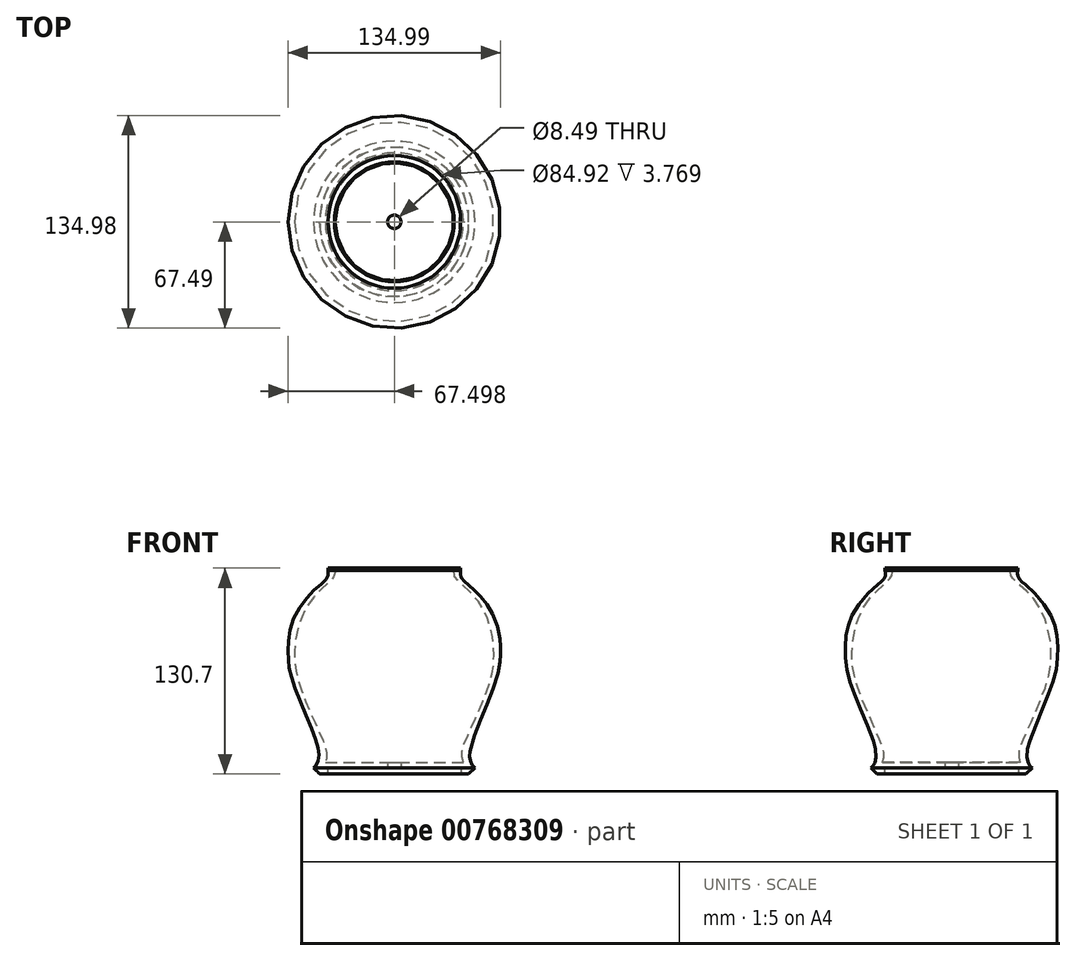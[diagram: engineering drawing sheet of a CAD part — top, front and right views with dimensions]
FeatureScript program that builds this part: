
annotation { "Feature Type Name" : "Feature", "Feature Type Description" : "" }
export const myFeature = defineFeature(function(context is Context, id is Id, definition is map)
    precondition{}
    {
        {
            var Q0;
            Q0=qCreatedBy(makeId("Front.planeOp"),FACE);
            var sketch = newSketch(context, id + "F0", { "sketchPlane" : qUnion([Q0])});
            skFitSpline(sketch, "E0", {"points": [v(87.17, 77.75) * mm, v(87.17, 72.81) * mm, v(102.26, 57.15) * mm, v(112.41, 25.24) * mm, v(108.06, 0) * mm, v(95.88, -28.43) * mm, v(92.1, -40.03) * mm, v(92.98, -45.55) * mm], "startDerivative": vector(-17.62, -61.82) * mm, "endDerivative": vector(18.04, -64.32) * mm});
            skLineSegment(sketch, "E1", {"start": v(92.98, -45.55) * mm, "end": v(53.4, -45.55) * mm});
            skLineSegment(sketch, "E2", {"start": v(53.4, -45.55) * mm, "end": v(53.4, -49.19) * mm});
            skLineSegment(sketch, "E3", {"start": v(53.4, -49.19) * mm, "end": v(91.62, -49.19) * mm});
            skLineSegment(sketch, "E4", {"start": v(91.62, -49.19) * mm, "end": v(91.62, -52.95) * mm});
            skLineSegment(sketch, "E5", {"start": v(91.62, -52.95) * mm, "end": v(96.43, -52.95) * mm});
            skLineSegment(sketch, "E6", {"start": v(96.43, -52.95) * mm, "end": v(100.45, -49.19) * mm});
            skFitSpline(sketch, "E7", {"points": [v(100.45, -49.19) * mm, v(98.45, -46.93) * mm, v(96.9, -41.33) * mm, v(100.45, -27.58) * mm, v(114.12, 7.38) * mm, v(116.6, 22.42) * mm, v(113.55, 44.68) * mm, v(98.33, 65.42) * mm, v(91.48, 71.9) * mm, v(91.29, 76.27) * mm], "startDerivative": vector(-39.93, 36.42) * mm, "endDerivative": vector(10.24, 71.22) * mm});
            skLineSegment(sketch, "E8", {"start": v(87.17, 77.75) * mm, "end": v(91.29, 77.75) * mm});
            skLineSegment(sketch, "E9", {"start": v(91.29, 77.75) * mm, "end": v(91.29, 76.27) * mm});
            skLineSegment(sketch, "E10", {"start": v(49.16, -62.85) * mm, "end": v(49.16, 92.7) * mm});
            skSolve(sketch);
        }
        {
            var Q0;
            Q0=makeQuery(id+"F0.imprint","IMPRINT",FACE,{"disambiguationData":[TD([[makeQuery(id+"F0.imprint","IMPRINT",EDGE,{"derivedFrom":sQuery(id+"F0.wireOp",EDGE,"E0")}),1.0]])]});
            var Q1;
            Q1=sQuery(id+"F0.wireOp",EDGE,"E10");
            revolve(context, id + "F1", {"surfaceOperationType" : NewSurfaceOperationType.NEW, "entities" : qUnion([Q0]), "axis" : qUnion([Q1]), "revolveType" : RevolveType.FULL});
        }
    });
